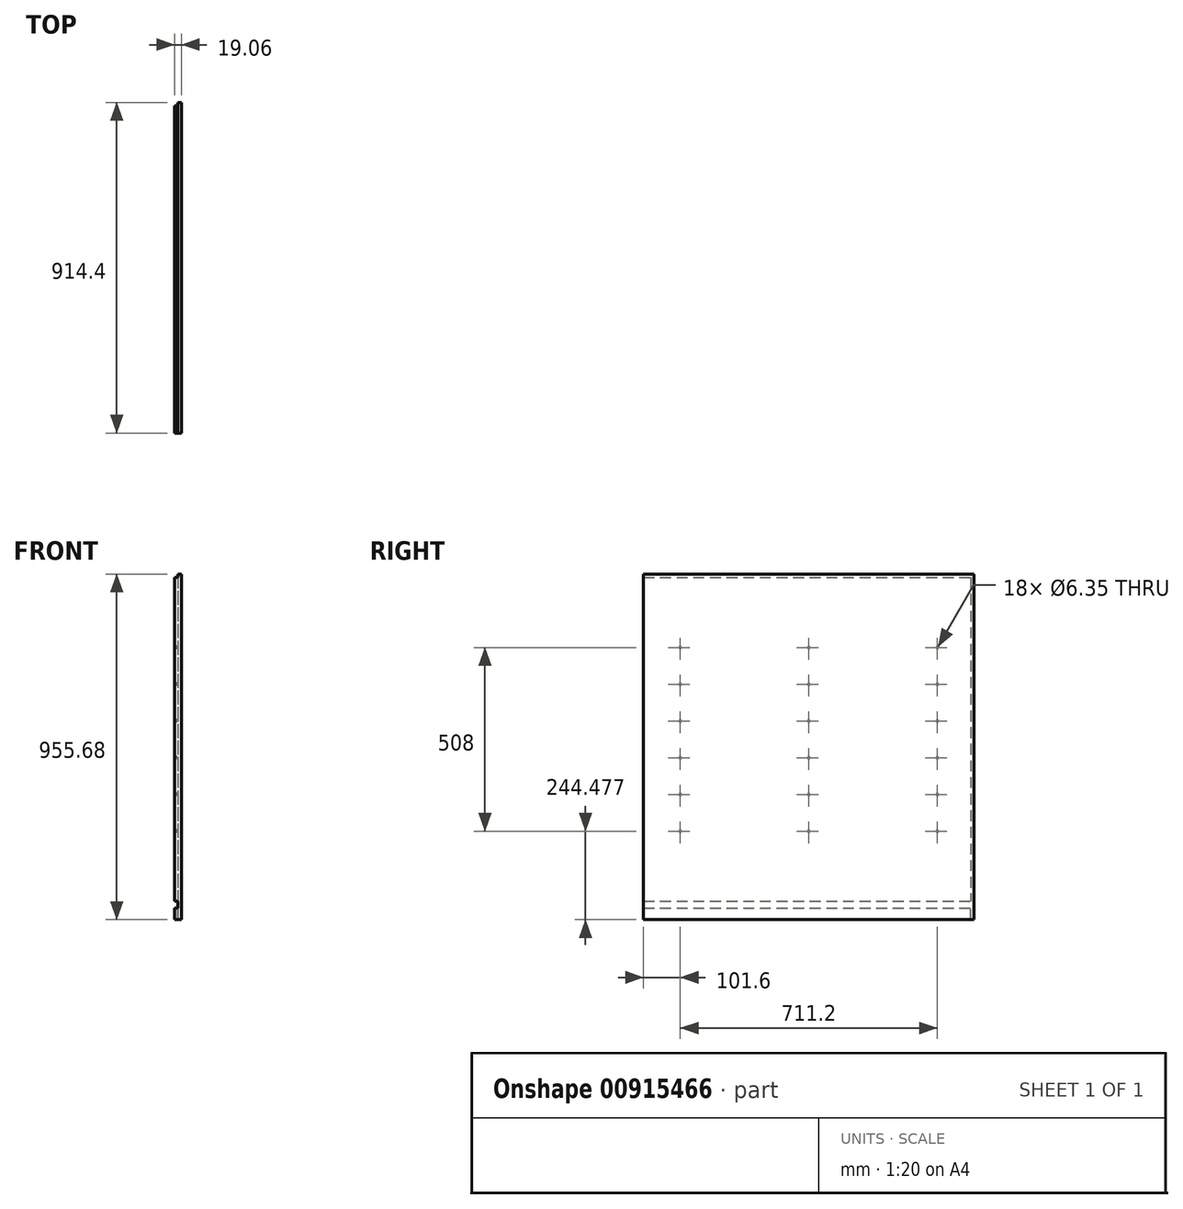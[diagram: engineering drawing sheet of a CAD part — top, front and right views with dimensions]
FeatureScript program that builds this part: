
annotation { "Feature Type Name" : "Feature", "Feature Type Description" : "" }
export const myFeature = defineFeature(function(context is Context, id is Id, definition is map)
    precondition{}
    {
        {
            var Q0;
            Q0=qCreatedBy(makeId("Right.planeOp"),FACE);
            var sketch = newSketch(context, id + "F0", { "sketchPlane" : qUnion([Q0])});
            skLineSegment(sketch, "E0.bottom", {"start": v(457.2, 477.84) * mm, "end": v(-457.2, 477.84) * mm});
            skLineSegment(sketch, "E0.top", {"start": v(457.2, -477.84) * mm, "end": v(-457.2, -477.84) * mm});
            skLineSegment(sketch, "E0.left", {"start": v(457.2, 477.84) * mm, "end": v(457.2, -477.84) * mm});
            skLineSegment(sketch, "E0.right", {"start": v(-457.2, 477.84) * mm, "end": v(-457.2, -477.84) * mm});
            skPoint(sketch, "E0.middle", {"position": v(0, 0) * mm});
            skSolve(sketch);
        }
        {
            var Q0;
            Q0=makeQuery(id+"F0.imprint","IMPRINT",FACE,{"disambiguationData":[TD([[makeQuery(id+"F0.imprint","IMPRINT",EDGE,{"derivedFrom":sQuery(id+"F0.wireOp",EDGE,"E0.bottom")}),1.0]])]});
            var sketch = newSketch(context, id + "F1", { "sketchPlane" : qUnion([Q0])});
            skLineSegment(sketch, "E1.bottom", {"start": v(-457.2, 468.31) * mm, "end": v(447.68, 468.31) * mm});
            skLineSegment(sketch, "E1.top", {"start": v(-457.2, -427.04) * mm, "end": v(447.68, -427.04) * mm});
            skLineSegment(sketch, "E1.left", {"start": v(-457.2, 468.31) * mm, "end": v(-457.2, -427.04) * mm});
            skLineSegment(sketch, "E1.right", {"start": v(447.68, 468.31) * mm, "end": v(447.68, -427.04) * mm});
            skLineSegment(sketch, "E2.bottom", {"start": v(-457.2, -477.84) * mm, "end": v(447.68, -477.84) * mm});
            skLineSegment(sketch, "E2.top", {"start": v(-457.2, -446.09) * mm, "end": v(447.68, -446.09) * mm});
            skLineSegment(sketch, "E2.left", {"start": v(-457.2, -477.84) * mm, "end": v(-457.2, -446.09) * mm});
            skLineSegment(sketch, "E2.right", {"start": v(447.68, -477.84) * mm, "end": v(447.68, -446.09) * mm});
            skSolve(sketch);
        }
        {
            var Q0;
            Q0=makeQuery(id+"F0.imprint","IMPRINT",FACE,{"disambiguationData":[TD([[makeQuery(id+"F0.imprint","IMPRINT",EDGE,{"derivedFrom":sQuery(id+"F0.wireOp",EDGE,"E0.bottom")}),1.0]])]});
            extrude(context, id + "F2", {"entities" : qUnion([Q0]), "depth" : 9.52 * mm, "offsetDistance" : 25.4 * mm});
        }
        {
            var Q0;
            Q0 = qSketchRegion(id + "F1", true);
            extrude(context, id + "F3", {"entities" : qUnion([Q0]), "operationType" : NewBodyOperationType.ADD, "oppositeDirection" : true, "depth" : 9.52 * mm, "offsetDistance" : 25.4 * mm});
        }
        {
            var Q0;
            Q0=makeQuery(id+"F3.opExtrude","CAP_FACE",FACE,{"disambiguationData":[OSD([sQuery(id+"F1.wireOp",EDGE,"E1.bottom"),sQuery(id+"F1.wireOp",EDGE,"E1.top"),sQuery(id+"F1.wireOp",EDGE,"E1.left"),sQuery(id+"F1.wireOp",EDGE,"E1.right")])],"isStart":false});
            var sketch = newSketch(context, id + "F4", { "sketchPlane" : qUnion([Q0])});
            skPoint(sketch, "E3", {"position": v(355.6, 274.64) * mm});
            skPoint(sketch, "E4.0.1.0", {"position": v(355.6, 173.04) * mm});
            skPoint(sketch, "E4.0.2.0", {"position": v(355.6, 71.44) * mm});
            skPoint(sketch, "E4.0.3.0", {"position": v(355.6, -30.16) * mm});
            skPoint(sketch, "E4.0.4.0", {"position": v(355.6, -131.76) * mm});
            skPoint(sketch, "E4.0.5.0", {"position": v(355.6, -233.36) * mm});
            skPoint(sketch, "E4.1.0.0", {"position": v(0, 274.64) * mm});
            skPoint(sketch, "E4.1.1.0", {"position": v(0, 173.04) * mm});
            skPoint(sketch, "E4.1.2.0", {"position": v(0, 71.44) * mm});
            skPoint(sketch, "E4.1.3.0", {"position": v(0, -30.16) * mm});
            skPoint(sketch, "E4.1.4.0", {"position": v(0, -131.76) * mm});
            skPoint(sketch, "E4.1.5.0", {"position": v(0, -233.36) * mm});
            skPoint(sketch, "E4.2.0.0", {"position": v(-355.6, 274.64) * mm});
            skPoint(sketch, "E4.2.1.0", {"position": v(-355.6, 173.04) * mm});
            skPoint(sketch, "E4.2.2.0", {"position": v(-355.6, 71.44) * mm});
            skPoint(sketch, "E4.2.3.0", {"position": v(-355.6, -30.16) * mm});
            skPoint(sketch, "E4.2.4.0", {"position": v(-355.6, -131.76) * mm});
            skPoint(sketch, "E4.2.5.0", {"position": v(-355.6, -233.36) * mm});
            skLineSegment(sketch, "E4.direction1", {"start": v(355.6, 274.64) * mm, "end": v(0, 274.64) * mm, "construction": true});
            skLineSegment(sketch, "E4.direction2", {"start": v(355.6, 274.64) * mm, "end": v(355.6, 173.04) * mm, "construction": true});
            skSolve(sketch);
        }
        {
            var Q0;
            Q0=sQuery(id+"F4.wireOp",VERTEX,"E4.2.0.0");
            var Q1;
            Q1=sQuery(id+"F4.wireOp",VERTEX,"E4.0.5.0");
            var Q2;
            Q2=sQuery(id+"F4.wireOp",VERTEX,"E4.2.3.0");
            var Q3;
            Q3=sQuery(id+"F4.wireOp",VERTEX,"E4.0.2.0");
            var Q4;
            Q4=sQuery(id+"F4.wireOp",VERTEX,"E4.0.3.0");
            var Q5;
            Q5=sQuery(id+"F4.wireOp",VERTEX,"E4.1.3.0");
            var Q6;
            Q6=sQuery(id+"F4.wireOp",VERTEX,"E4.1.5.0");
            var Q7;
            Q7=sQuery(id+"F4.wireOp",VERTEX,"E3");
            var Q8;
            Q8=sQuery(id+"F4.wireOp",VERTEX,"E4.1.4.0");
            var Q9;
            Q9=sQuery(id+"F4.wireOp",VERTEX,"E4.1.2.0");
            var Q10;
            Q10=sQuery(id+"F4.wireOp",VERTEX,"E4.2.2.0");
            var Q11;
            Q11=sQuery(id+"F4.wireOp",VERTEX,"E4.2.4.0");
            var Q12;
            Q12=sQuery(id+"F4.wireOp",VERTEX,"E4.1.0.0");
            var Q13;
            Q13=sQuery(id+"F4.wireOp",VERTEX,"E4.2.1.0");
            var Q14;
            Q14=sQuery(id+"F4.wireOp",VERTEX,"E4.0.1.0");
            var Q15;
            Q15=sQuery(id+"F4.wireOp",VERTEX,"E4.1.1.0");
            var Q16;
            Q16=sQuery(id+"F4.wireOp",VERTEX,"E4.0.4.0");
            var Q17;
            Q17=sQuery(id+"F4.wireOp",VERTEX,"E4.2.5.0");
            var Q18;
            Q18=makeQuery(id+"F2.opExtrude","SWEPT_BODY",BODY,{"disambiguationData":[OSD([sQuery(id+"F0.wireOp",EDGE,"E0.bottom"),sQuery(id+"F0.wireOp",EDGE,"E0.top"),sQuery(id+"F0.wireOp",EDGE,"E0.left"),sQuery(id+"F0.wireOp",EDGE,"E0.right")])]});
            hole(context, id + "F5", {"style" : HoleStyle.SIMPLE, "endStyle" : HoleEndStyle.BLIND, "holeDiameter" : 6.35 * mm, "majorDiameter" : 6.35 * mm, "holeDepth" : 6.35 * mm, "isTappedThrough" : true, "tappedDepth" : 12.7 * mm, "tapClearance" : 3, "startFromSketch" : true, "locations" : qUnion([Q0, Q1, Q2, Q3, Q4, Q5, Q6, Q7, Q8, Q9, Q10, Q11, Q12, Q13, Q14, Q15, Q16, Q17]), "scope" : qUnion([Q18])});
        }
    });
